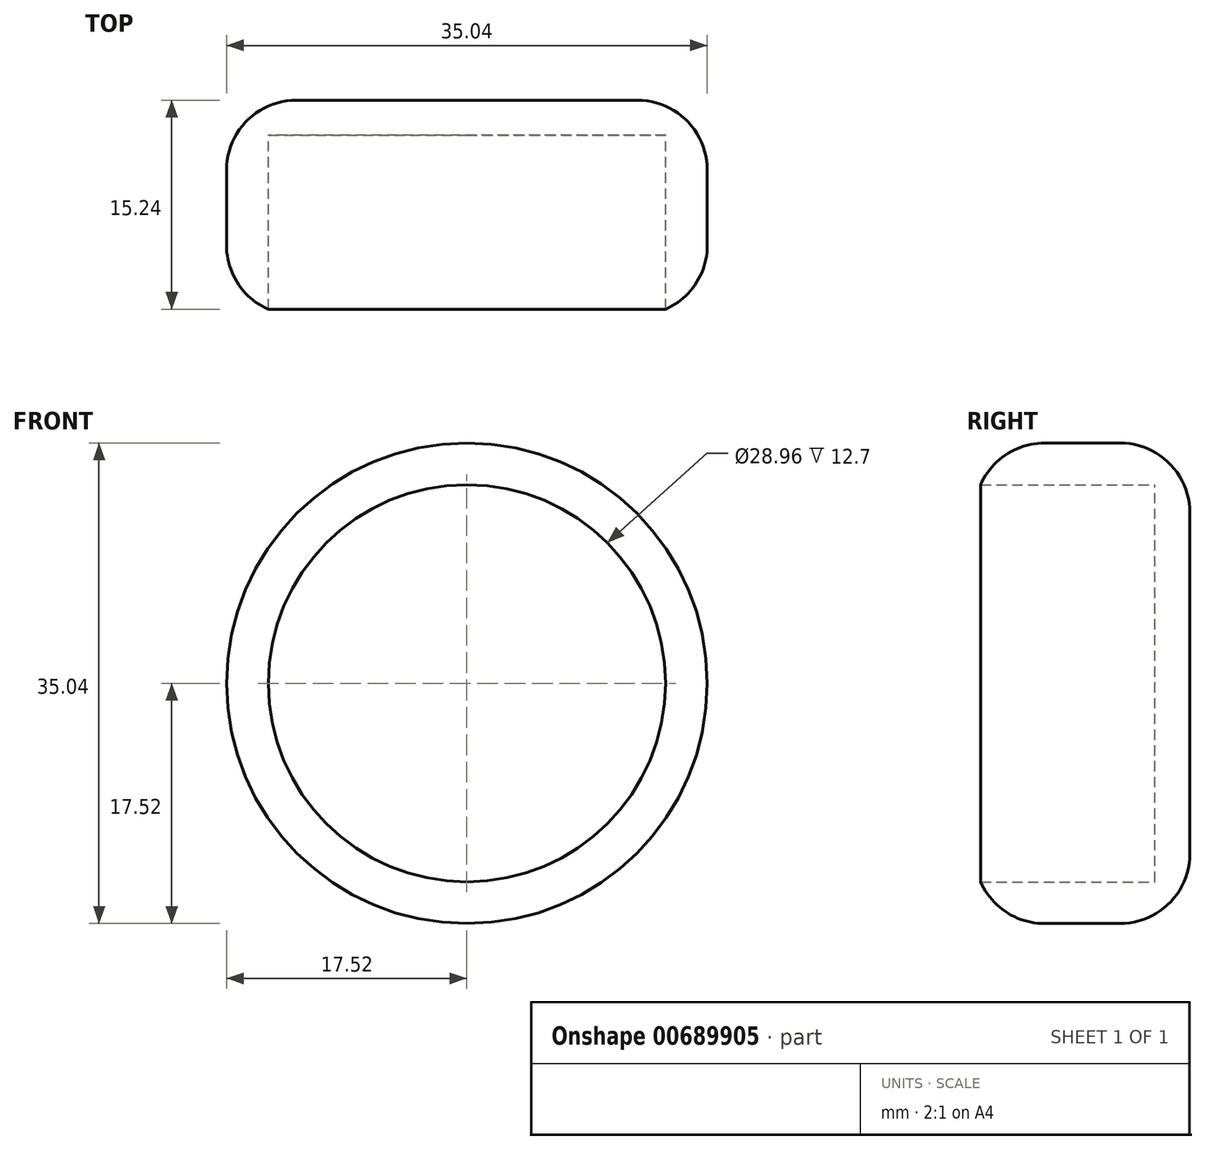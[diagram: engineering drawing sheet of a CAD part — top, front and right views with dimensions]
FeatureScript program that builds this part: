
annotation { "Feature Type Name" : "Feature", "Feature Type Description" : "" }
export const myFeature = defineFeature(function(context is Context, id is Id, definition is map)
    precondition{}
    {
        {
            var Q0;
            Q0=qCreatedBy(makeId("Front.planeOp"),FACE);
            var sketch = newSketch(context, id + "F0", { "sketchPlane" : qUnion([Q0])});
            skCircle(sketch, "E0", {"center": v(0, 0) * mm, "radius": 14.48 * mm});
            skCircle(sketch, "E1", {"center": v(0, 0) * mm, "radius": 17.52 * mm});
            skSolve(sketch);
        }
        {
            var Q0;
            Q0=makeQuery(id+"F0.imprint","IMPRINT",FACE,{"disambiguationData":[TD([[makeQuery(id+"F0.imprint","IMPRINT",EDGE,{"derivedFrom":sQuery(id+"F0.wireOp",EDGE,"E0")}),1.0]])]});
            extrude(context, id + "F1", {"entities" : qUnion([Q0]), "depth" : 2.54 * mm, "offsetDistance" : 25.4 * mm});
        }
        {
            var Q0;
            Q0 = qSketchRegion(id + "F0", true);
            extrude(context, id + "F2", {"entities" : qUnion([Q0]), "operationType" : NewBodyOperationType.ADD, "depth" : 15.24 * mm, "offsetDistance" : 25.4 * mm});
        }
        {
            var Q0;
            Q0=makeQuery(id+"F2.opExtrude","SWEPT_FACE",FACE,{"disambiguationData":[OSD([sQuery(id+"F0.wireOp",EDGE,"E1")])]});
            fillet(context, id + "F3", {"entities" : qUnion([Q0]), "radius" : 5.08 * mm, "tangentPropagation" : true, "allowEdgeOverflow" : false});
        }
    });
